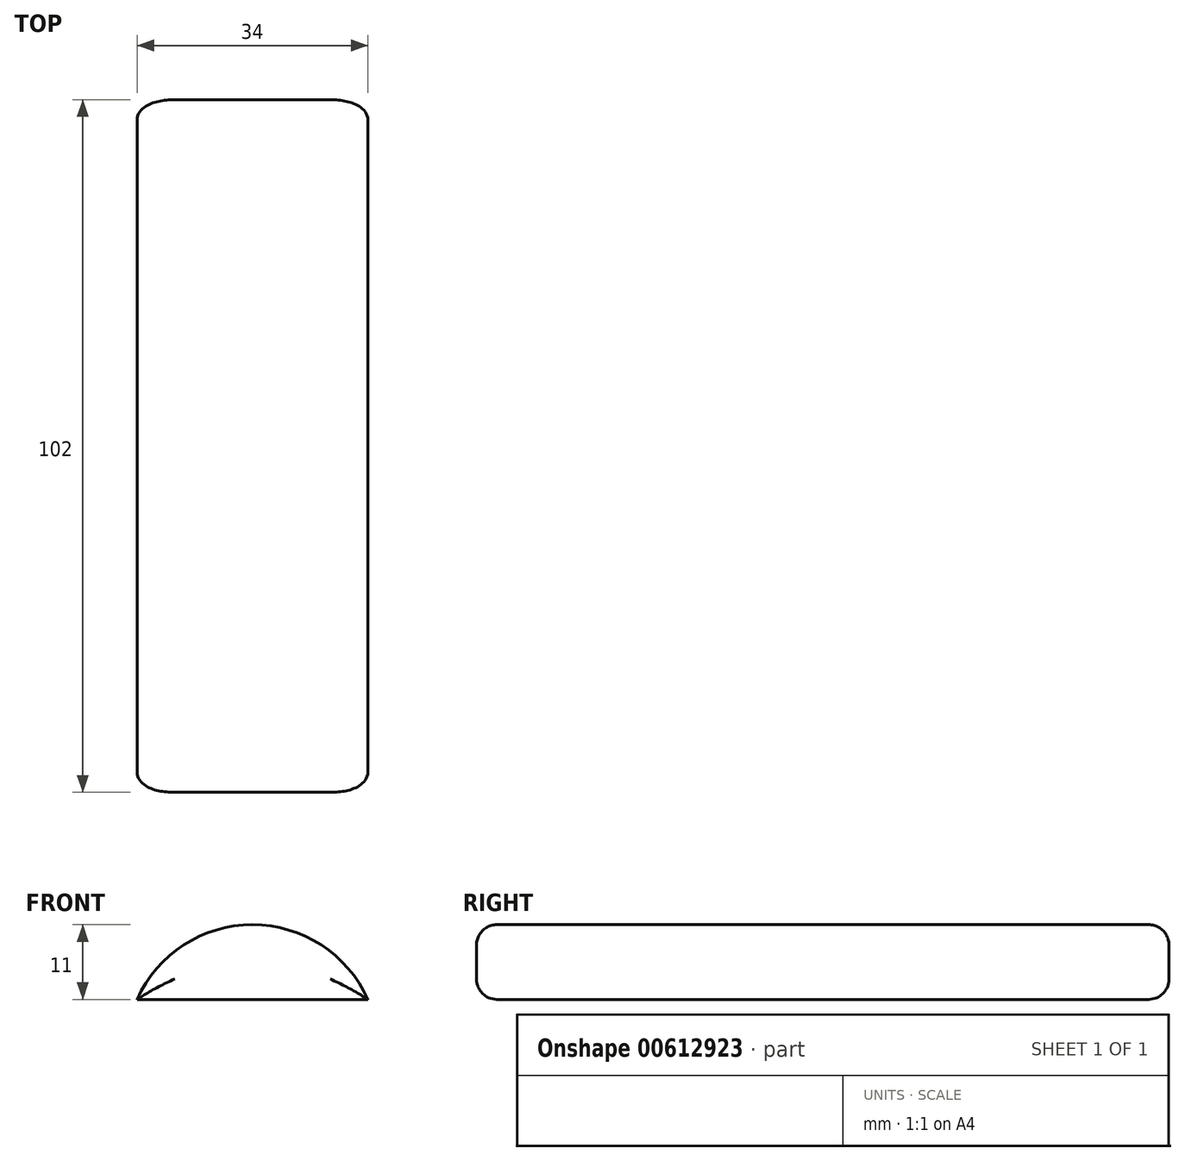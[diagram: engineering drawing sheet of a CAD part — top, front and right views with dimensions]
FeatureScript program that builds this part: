
annotation { "Feature Type Name" : "Feature", "Feature Type Description" : "" }
export const myFeature = defineFeature(function(context is Context, id is Id, definition is map)
    precondition{}
    {
        {
            var Q0;
            Q0=qCreatedBy(makeId("Front.planeOp"),FACE);
            var sketch = newSketch(context, id + "F0", { "sketchPlane" : qUnion([Q0])});
            skPoint(sketch, "E0.middle", {"position": v(0, 0) * mm});
            skLineSegment(sketch, "E1", {"start": v(-17, -7) * mm, "end": v(-17, -4) * mm});
            skLineSegment(sketch, "E2", {"start": v(17, -7) * mm, "end": v(17, -4) * mm});
            skLineSegment(sketch, "E3", {"start": v(-17, -7) * mm, "end": v(17, -7) * mm});
            skLineSegment(sketch, "E4", {"start": v(0, 0) * mm, "end": v(0, 7) * mm});
            skLineSegment(sketch, "E5", {"start": v(0, 0) * mm, "end": v(0, -7) * mm});
            skLineSegment(sketch, "E6.bottom", {"start": v(-17, -4) * mm, "end": v(17, -4) * mm});
            skLineSegment(sketch, "E6.left", {"start": v(-17, -4) * mm, "end": v(-17, -7) * mm});
            skLineSegment(sketch, "E6.right", {"start": v(17, -4) * mm, "end": v(17, -7) * mm});
            skArc(sketch, "E7", {"start": v(17, -4) * mm, "mid": v(0, 7) * mm, "end": v(-17, -4) * mm});
            skSolve(sketch);
        }
        {
            var Q0;
            {var subQ0=sQuery(id+"F0.wireOp",EDGE,"E4");Q0=makeQuery(id+"F0.imprint","IMPRINT",FACE,{"disambiguationData":[TD([[makeQuery(id+"F0.imprint","IMPRINT",EDGE,{"derivedFrom":subQ0}),1.0]])]});}
            var Q1;
            {var subQ0=sQuery(id+"F0.wireOp",EDGE,"E4");Q1=makeQuery(id+"F0.imprint","IMPRINT",FACE,{"disambiguationData":[TD([[makeQuery(id+"F0.imprint","IMPRINT",EDGE,{"derivedFrom":subQ0}),-1.0]])]});}
            var Q2;
            {var subQ5=sQuery(id+"F0.wireOp",EDGE,"E6.left");Q2=makeQuery(id+"F0.imprint","IMPRINT",FACE,{"disambiguationData":[TD([[makeQuery(id+"F0.imprint","IMPRINT",EDGE,{"derivedFrom":subQ5}),1.0]])]});}
            var Q3;
            {var subQ5=sQuery(id+"F0.wireOp",EDGE,"E6.right");Q3=makeQuery(id+"F0.imprint","IMPRINT",FACE,{"disambiguationData":[TD([[makeQuery(id+"F0.imprint","IMPRINT",EDGE,{"derivedFrom":subQ5}),-1.0]])]});}
            extrude(context, id + "F1", {"entities" : qUnion([Q0, Q1, Q2, Q3]), "depth" : 102 * mm, "offsetDistance" : 25 * mm});
        }
        {
            var Q0;
            Q0=makeQuery(id+"F1.opExtrude","CAP_FACE",FACE,{"disambiguationData":[OSD([sQuery(id+"F0.wireOp",EDGE,"E3"),sQuery(id+"F0.wireOp",EDGE,"E6.left"),sQuery(id+"F0.wireOp",EDGE,"E6.right"),sQuery(id+"F0.wireOp",EDGE,"E7")])],"isStart":false});
            var Q1;
            Q1=makeQuery(id+"F1.opExtrude","CAP_FACE",FACE,{"disambiguationData":[OSD([sQuery(id+"F0.wireOp",EDGE,"E3"),sQuery(id+"F0.wireOp",EDGE,"E6.left"),sQuery(id+"F0.wireOp",EDGE,"E6.right"),sQuery(id+"F0.wireOp",EDGE,"E7")])],"isStart":true});
            fillet(context, id + "F2", {"entities" : qUnion([Q0, Q1]), "radius" : 3 * mm, "tangentPropagation" : true, "allowEdgeOverflow" : false});
        }
    });
